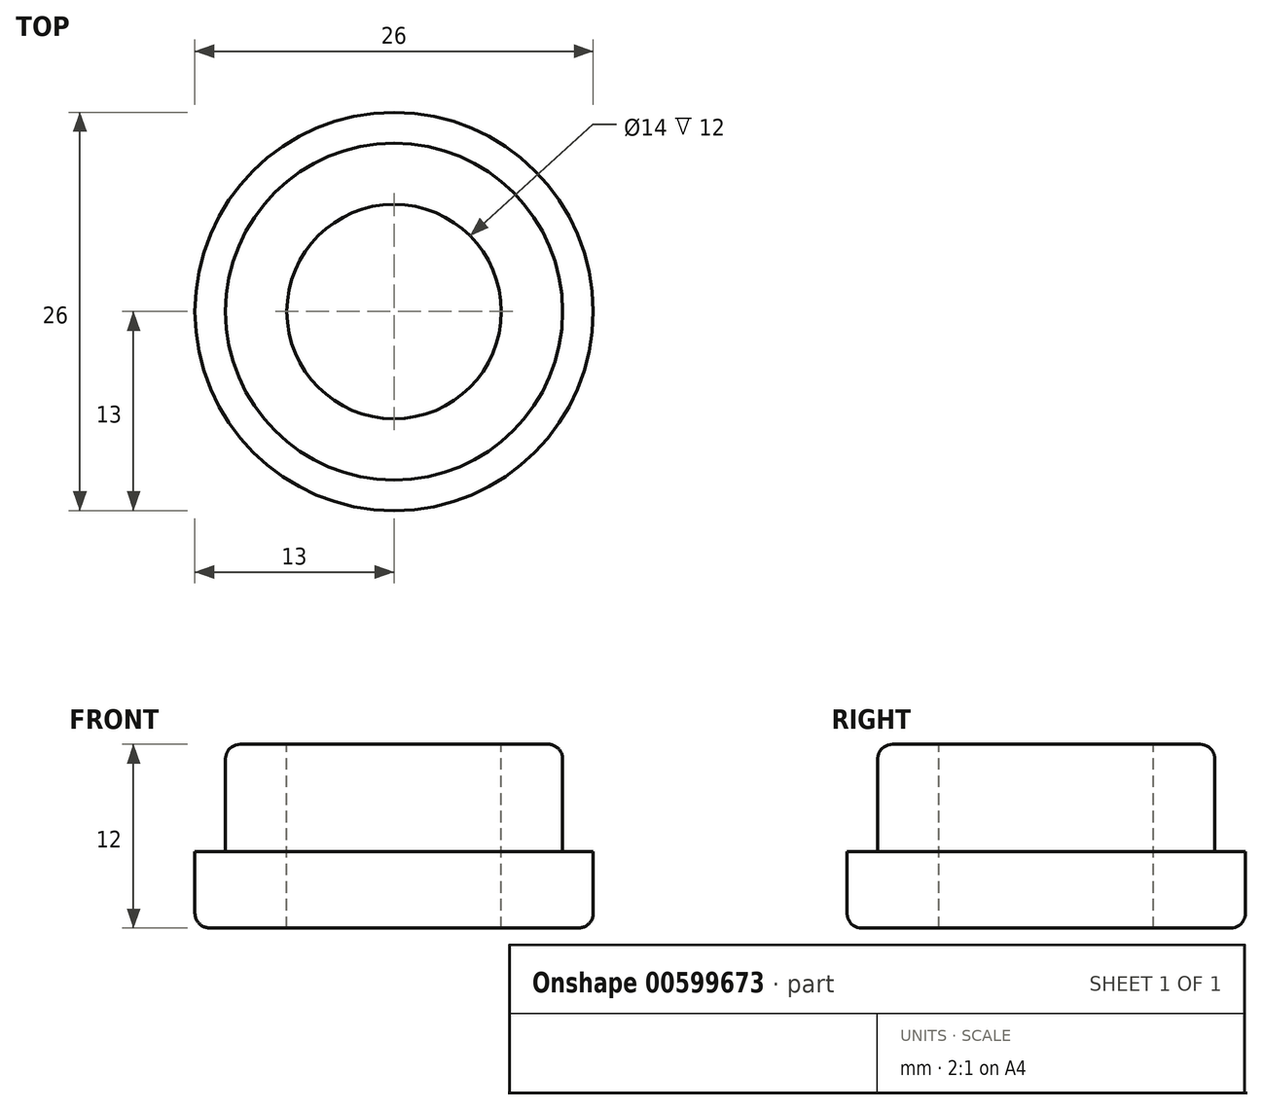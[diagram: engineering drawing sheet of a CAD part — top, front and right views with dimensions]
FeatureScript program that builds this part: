
annotation { "Feature Type Name" : "Feature", "Feature Type Description" : "" }
export const myFeature = defineFeature(function(context is Context, id is Id, definition is map)
    precondition{}
    {
        {
            var Q0;
            Q0=qCreatedBy(makeId("Top.planeOp"),FACE);
            var sketch = newSketch(context, id + "F0", { "sketchPlane" : qUnion([Q0])});
            skCircle(sketch, "E0", {"center": v(0, 0) * mm, "radius": 13 * mm});
            skSolve(sketch);
        }
        {
            var Q0;
            Q0=makeQuery(id+"F0.imprint","IMPRINT",FACE,{"disambiguationData":[TD([[makeQuery(id+"F0.imprint","IMPRINT",EDGE,{"derivedFrom":sQuery(id+"F0.wireOp",EDGE,"E0")}),1.0]])]});
            extrude(context, id + "F1", {"entities" : qUnion([Q0]), "depth" : 5 * mm, "offsetDistance" : 25 * mm});
        }
        {
            var Q0;
            Q0=makeQuery(id+"F1.opExtrude","CAP_FACE",FACE,{"disambiguationData":[OSD([sQuery(id+"F0.wireOp",EDGE,"E0")])],"isStart":false});
            var sketch = newSketch(context, id + "F2", { "sketchPlane" : qUnion([Q0])});
            skCircle(sketch, "E1", {"center": v(0, 0) * mm, "radius": 11 * mm});
            skSolve(sketch);
        }
        {
            var Q0;
            Q0=makeQuery(id+"F2.imprint","IMPRINT",FACE,{"disambiguationData":[TD([[makeQuery(id+"F2.imprint","IMPRINT",EDGE,{"derivedFrom":sQuery(id+"F2.wireOp",EDGE,"E1")}),1.0]])]});
            extrude(context, id + "F3", {"entities" : qUnion([Q0]), "operationType" : NewBodyOperationType.ADD, "depth" : 7 * mm, "offsetDistance" : 25 * mm});
        }
        {
            var Q0;
            Q0=makeQuery(id+"F3.opExtrude","CAP_FACE",FACE,{"disambiguationData":[OSD([sQuery(id+"F2.wireOp",EDGE,"E1")])],"isStart":false});
            var sketch = newSketch(context, id + "F4", { "sketchPlane" : qUnion([Q0])});
            skCircle(sketch, "E2", {"center": v(0, 0) * mm, "radius": 7 * mm});
            skSolve(sketch);
        }
        {
            var Q0;
            Q0=sQuery(id+"F4.wireOp",VERTEX,"E2.center");
            var Q1;
            Q1=makeQuery(id+"F1.opExtrude","SWEPT_BODY",BODY,{"disambiguationData":[OSD([sQuery(id+"F0.wireOp",EDGE,"E0")])]});
            hole(context, id + "F5", {"style" : HoleStyle.C_BORE, "endStyle" : HoleEndStyle.THROUGH, "holeDiameter" : 14 * mm, "cBoreDiameter" : 14 * mm, "cBoreDepth" : 14 * mm, "majorDiameter" : 5 * mm, "isTappedThrough" : true, "tappedDepth" : 12 * mm, "tapClearance" : 3, "startFromSketch" : true, "locations" : qUnion([Q0]), "scope" : qUnion([Q1])});
        }
        {
            var Q0;
            Q0=makeQuery(id+"F3.opExtrude","CAP_EDGE",EDGE,{"disambiguationData":[OSD([sQuery(id+"F2.wireOp",EDGE,"E1")])],"isStart":false});
            fillet(context, id + "F6", {"entities" : qUnion([Q0]), "radius" : 0.97 * mm, "tangentPropagation" : true, "allowEdgeOverflow" : false});
        }
        {
            var Q0;
            Q0=makeQuery(id+"F1.opExtrude","CAP_EDGE",EDGE,{"disambiguationData":[OSD([sQuery(id+"F0.wireOp",EDGE,"E0")])],"isStart":true});
            fillet(context, id + "F7", {"entities" : qUnion([Q0]), "radius" : 0.97 * mm, "tangentPropagation" : true, "allowEdgeOverflow" : false});
        }
    });
